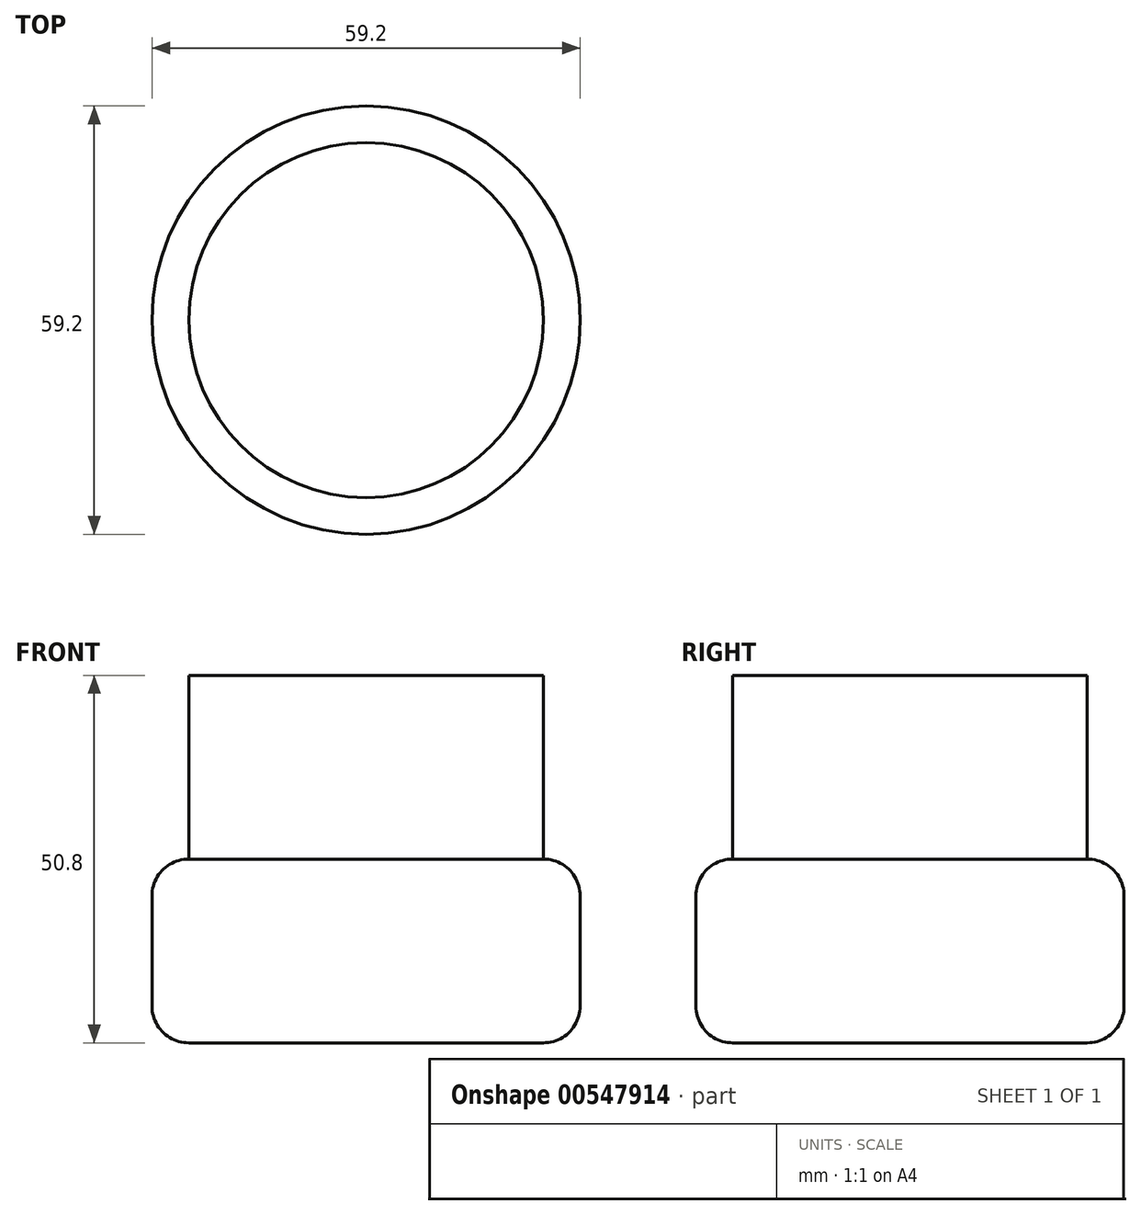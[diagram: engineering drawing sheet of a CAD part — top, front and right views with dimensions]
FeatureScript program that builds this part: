
annotation { "Feature Type Name" : "Feature", "Feature Type Description" : "" }
export const myFeature = defineFeature(function(context is Context, id is Id, definition is map)
    precondition{}
    {
        {
            var Q0;
            Q0=qCreatedBy(makeId("Top.planeOp"),FACE);
            var sketch = newSketch(context, id + "F0", { "sketchPlane" : qUnion([Q0])});
            skCircle(sketch, "E0", {"center": v(0, 0) * mm, "radius": 29.6 * mm});
            skSolve(sketch);
        }
        {
            var Q0;
            Q0=makeQuery(id+"F0.imprint","IMPRINT",FACE,{"disambiguationData":[TD([[makeQuery(id+"F0.imprint","IMPRINT",EDGE,{"derivedFrom":sQuery(id+"F0.wireOp",EDGE,"E0")}),1.0]])]});
            extrude(context, id + "F1", {"entities" : qUnion([Q0]), "depth" : 25.4 * mm, "offsetDistance" : 25.4 * mm, "symmetric" : true});
        }
        {
            var Q0;
            Q0=makeQuery(id+"F1.opExtrude","CAP_EDGE",EDGE,{"disambiguationData":[OSD([sQuery(id+"F0.wireOp",EDGE,"E0")])],"isStart":false});
            var Q1;
            Q1=makeQuery(id+"F1.opExtrude","CAP_EDGE",EDGE,{"disambiguationData":[OSD([sQuery(id+"F0.wireOp",EDGE,"E0")])],"isStart":true});
            fillet(context, id + "F2", {"entities" : qUnion([Q0, Q1]), "radius" : 5.08 * mm, "tangentPropagation" : true, "allowEdgeOverflow" : false});
        }
        {
            var Q0;
            Q0=makeQuery(id+"F1.opExtrude","CAP_FACE",FACE,{"disambiguationData":[OSD([sQuery(id+"F0.wireOp",EDGE,"E0")])],"isStart":false});
            extrude(context, id + "F3", {"entities" : qUnion([Q0]), "operationType" : NewBodyOperationType.ADD, "depth" : 25.4 * mm, "offsetDistance" : 25.4 * mm});
        }
    });
